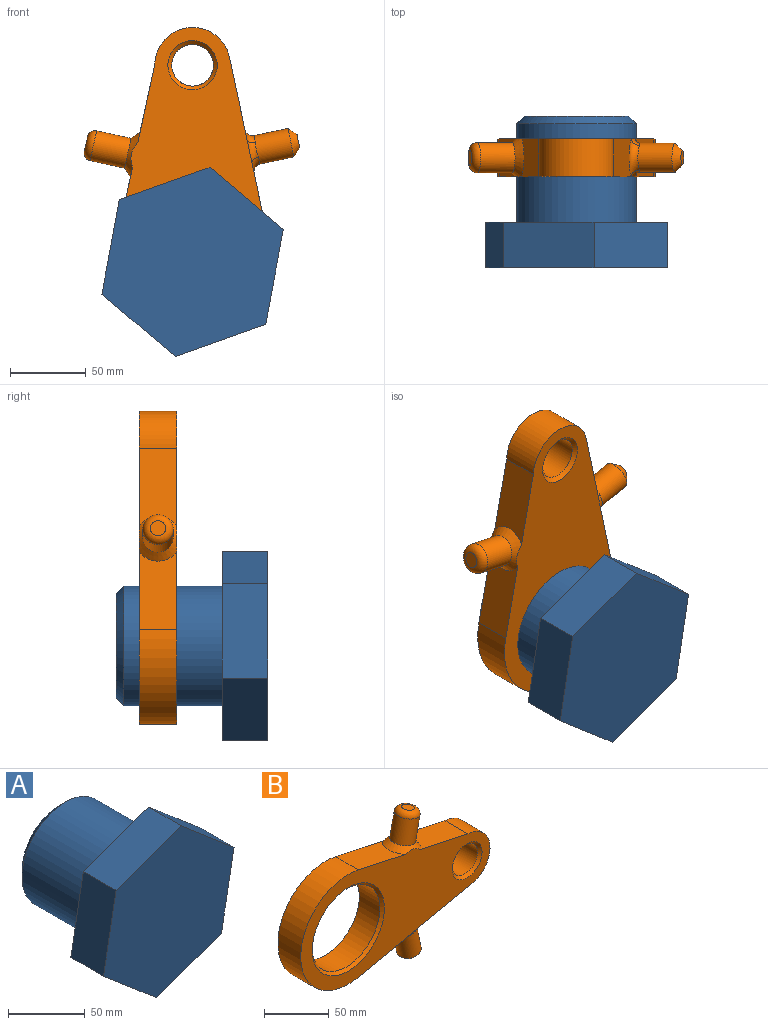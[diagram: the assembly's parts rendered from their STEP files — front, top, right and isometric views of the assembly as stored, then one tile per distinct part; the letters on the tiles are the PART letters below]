
ASSEMBLY  parts=2 mates=1
PART A: 11 faces, bbox 119.9x100.3x125.1 mm
  f0: cylinder r=39.5mm len=79mm, axis (0,1,0), area 16206.5mm2, adj f9,f10
  f1: plane 69x69mm, normal (0,1,0), area 3739.3mm2, adj f10
  f2: plane 59.93x30mm, normal (0.33,0,-0.94), area 1907.8mm2, adj f3,f7,f8,f9
  f3: plane 62.54x30mm, normal (0.98,0,-0.18), area 1907.8mm2, adj f2,f4,f8,f9
  f4: plane 48.39x41.26mm, normal (0.65,0,0.76), area 1907.8mm2, adj f3,f5,f8,f9
  f5: plane 59.93x30mm, normal (-0.33,0,0.94), area 1907.8mm2, adj f4,f6,f8,f9
  f6: plane 62.54x30mm, normal (-0.98,0,0.18), area 1907.8mm2, adj f5,f7,f8,f9
  f7: plane 48.39x41.26mm, normal (-0.65,0,-0.76), area 1907.8mm2, adj f2,f6,f8,f9
  f8: plane 125.08x119.85mm, normal (0,-1,0), area 10506.9mm2, adj f2,f3,f4,f5,f6,f7
  f9: plane 125.08x119.85mm, normal (0,1,0), area 5605.3mm2, adj f0,f2,f3,f4,f5,f6,f7
  f10: cone r=39.5mm half-angle=45deg, axis (0,-1,0), area 1643.9mm2, adj f0,f1
PART B: 45 faces, bbox 211.4x41.3x146.9 mm
  f0: plane 32.56x32.56mm, normal (0,1,0), area 236.1mm2, adj f22,f42
  f1: plane 79x79mm, normal (0,1,0), area 600.8mm2, adj f8,f29
  f2: plane 54.83x25mm, normal (0.21,0,-0.98), area 1276.4mm2, adj f4,f9,f10,f18
  f3: plane 51.6x25mm, normal (0.21,0,0.98), area 1203.1mm2, adj f6,f9,f10,f13
  f4: cylinder r=25mm len=49.45mm, axis (0,-1,0), area 1815.6mm2, adj f2,f5,f9,f10
  f5: plane 51.6x25mm, normal (0.21,0,0.98), area 1203.1mm2, adj f4,f9,f10,f13
  f6: cylinder r=52mm len=104mm, axis (0,-1,0), area 4632.4mm2, adj f3,f7,f9,f10
  f7: plane 54.83x25mm, normal (0.21,0,-0.98), area 1276.4mm2, adj f6,f9,f10,f19
  f8: cylinder r=37mm len=74mm, axis (0,-1,0), area 5230.8mm2, adj f1,f43
  f9: plane 211.38x108.38mm, normal (0,1,0), area 1266mm2, adj f2,f3,f4,f5,f6,f7,f13,f17
  f10: plane 207.31x104.31mm, normal (0,-1,0), area 9724.4mm2, adj f2,f3,f4,f5,f6,f7,f13,f20
  f11: cylinder r=10.08mm len=27.03mm, axis (-0.21,0,-0.98), area 1476.4mm2, adj f13,f14
  f12: plane 10.17x9.94mm, normal (0.21,0,0.98), area 81.2mm2, adj f14
  f13: cone r=10.08mm half-angle=45deg, axis (-0.21,0,-0.98), area 475.3mm2, adj f3,f5,f9,f10,f11
  f14: torus R=5.08mm, axis (0.21,0,0.98), area 408mm2, adj f11,f12
  f15: cylinder r=9.59mm len=26.48mm, axis (-0.21,0,0.98), area 1386.2mm2, adj f17,f18,f19,f20,f21
  f16: plane 9.18x8.98mm, normal (0.21,0,-0.98), area 66.2mm2, adj f21
  f17: bspline ~16.08x7.75mm, area 75.6mm2, adj f9,f15,f18,f19
  f18: torus R=14.59mm, axis (0.21,0,-0.98), area 184.4mm2, adj f2,f15,f17,f20
  f19: torus R=14.59mm, axis (0.21,0,-0.98), area 184.4mm2, adj f7,f15,f17,f20
  f20: bspline ~16.08x7.65mm, area 75.6mm2, adj f10,f15,f18,f19
  f21: cone r=4.59mm half-angle=45deg, axis (-0.21,0,0.98), area 315.1mm2, adj f15,f16
  f22: cylinder r=13.78mm len=27.56mm, axis (0,1,0), area 1947.9mm2, adj f0,f44
  f23: plane 54.83x22.5mm, normal (-0.21,0,0.98), area 1140.5mm2, adj f9,f25,f30,f38
  f24: plane 53.59x22.5mm, normal (-0.21,0,-0.98), area 1102mm2, adj f9,f27,f30,f33
  f25: cylinder r=22.5mm len=44.51mm, axis (0,-1,0), area 1475.7mm2, adj f9,f23,f26,f30
  f26: plane 53.82x22.5mm, normal (-0.21,0,-0.98), area 1107.4mm2, adj f9,f25,f30,f33
  f27: cylinder r=49.5mm len=99mm, axis (0,-1,0), area 3968.7mm2, adj f9,f24,f28,f30
  f28: plane 54.83x22.5mm, normal (-0.21,0,0.98), area 1140.5mm2, adj f9,f27,f30,f39
  f29: cylinder r=39.5mm len=79mm, axis (0,-1,0), area 5584.2mm2, adj f1,f30
  f30: plane 203.02x100.02mm, normal (0,1,0), area 8511.4mm2, adj f23,f24,f25,f26,f27,f28,f29,f33
  f31: cylinder r=7.58mm len=26.99mm, axis (-0.21,0,-0.98), area 1159.7mm2, adj f33,f34
  f32: plane 10.17x9.94mm, normal (-0.21,0,-0.98), area 81.2mm2, adj f34
  f33: cone r=8.32mm half-angle=45deg, axis (-0.21,0,-0.98), area 543.5mm2, adj f9,f24,f26,f30,f31
  f34: torus R=5.08mm, axis (0.21,0,0.98), area 164.7mm2, adj f31,f32
  f35: cylinder r=7.09mm len=24.43mm, axis (-0.21,0,0.98), area 978.7mm2, adj f37,f38,f39,f40,f41
  f36: plane 7.11x6.96mm, normal (-0.21,0,0.98), area 39.7mm2, adj f41
  f37: bspline ~16.08x9.89mm, area 93.1mm2, adj f9,f35,f38,f39
  f38: torus R=14.59mm, axis (0.21,0,-0.98), area 232.4mm2, adj f23,f30,f35,f37,f40
  f39: torus R=14.59mm, axis (0.21,0,-0.98), area 232.4mm2, adj f28,f30,f35,f37,f40
  f40: bspline ~16.07x9.79mm, area 62.8mm2, adj f30,f35,f38,f39
  f41: cone r=2.82mm half-angle=45deg, axis (-0.21,0,0.98), area 167.3mm2, adj f35,f36
  f42: cylinder r=16.28mm len=32.56mm, axis (0,1,0), area 2301.3mm2, adj f0,f30
  f43: cone r=37mm half-angle=45deg, axis (0,-1,0), area 849.7mm2, adj f8,f10
  f44: cone r=13.78mm half-angle=45deg, axis (0,-1,0), area 333.8mm2, adj f10,f22
PLACE A t=(144.35,-42.06,1.94)mm
PLACE B rot(axis=(0,-1,0),90deg) t=(144.35,-82.21,1.94)mm
MATE fastened A.f0 <-> B.f8  axis (0,1,0) through (144.35,-79.71,1.94)mm
